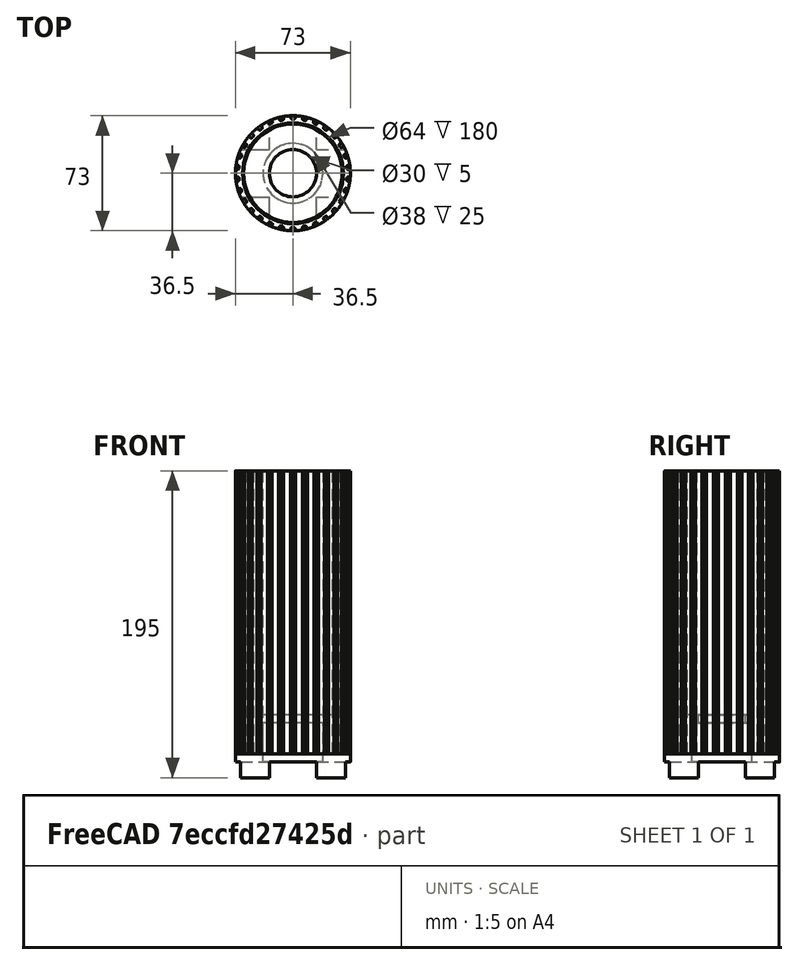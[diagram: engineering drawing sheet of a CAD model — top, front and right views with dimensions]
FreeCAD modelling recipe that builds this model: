
FCSTD DOCUMENT  (FreeCAD 0.15R4671 (Git))
Label: pica-small
License: All rights reserved
LicenseURL: http://en.wikipedia.org/wiki/All_rights_reserved
objects: Drawing::FeatureView×13, Part::Cylinder×7, Part::Cut×5, Drawing::FeatureViewPart×4, Part::MultiFuse×3, Part::Box×2, Part::Part2DObjectPython×1, PartDesign::Pad×1, Drawing::FeaturePage×1
note: 20 computed .brp shape members not serialized (recipe doc carries the construction recipe); baked Part::Feature solids carry a one-line shape summary decoded from their .brp

FEATURE [Part::Part2DObjectPython] InvoluteGear  # Draft 2D object (typed FeaturePython)
  ExternalGear = true
  HighPrecision = true
  Modules = 2.5
  NumberOfTeeth = 30
  PressureAngle = 20
FEATURE [PartDesign::Pad] Pad
  Length = 180
  Length2 = 100
  Sketch = -> InvoluteGear
  Type = 0
FEATURE [Part::Cylinder] Cylinder
  Angle = 360
  Height = 200
  Placement = pos=(0,0,-10) rot=(0,0,1;0rad)
  Radius = 32
FEATURE [Part::Cut] Cut  label="Final"
  Base = -> Pad
  Tool = -> Cylinder
FEATURE [Part::Cylinder] Cylinder001
  Angle = 360
  Height = 400
  Radius = 36.5
FEATURE [Part::Cylinder] Cylinder002
  Angle = 360
  Height = 400
  Radius = 100
FEATURE [Part::Cut] Cut001
  Base = -> Cylinder002
  Tool = -> Cylinder001
FEATURE [Part::Cut] Cut002  label="Shade"
  Base = -> Cut
  Placement = pos=(0,0,15) rot=(0,0,1;0rad)
  Tool = -> Cut001
FEATURE [Part::Cylinder] Cylinder003
  Angle = 360
  Height = 15
  Radius = 36.5
FEATURE [Part::Cylinder] Cylinder004
  Angle = 360
  Height = 40
  Radius = 31.3
FEATURE [Part::MultiFuse] Fusion  label="Base Fusion"
  Shapes = -> [Cylinder004,Cylinder003]
FEATURE [Part::Box] Box  label="Cube"
  Height = 10
  Length = 100
  Placement = pos=(-50,-15,0) rot=(0,0,1;0rad)
  Width = 30
FEATURE [Part::Box] Box001  label="Cube001"
  Height = 10
  Length = 100
  Placement = pos=(15,-50,0) rot=(0,0,1;1.5708rad)
  Width = 30
FEATURE [Part::MultiFuse] Fusion001  label="Feet Cutout Fusion"
  Shapes = -> [Box001,Box]
FEATURE [Part::Cut] Cut003  label="Plain Base"
  Base = -> Fusion
  Tool = -> Fusion001
FEATURE [Drawing::FeatureViewPart] FrontView  label="Shade Side"
  Direction = (0,-1,0)
  HiddenWidth = 0.15
  LineWidth = 0.35
  Rotation = 90
  ShowHiddenLines = true
  ShowSmoothLines = false
  Source = -> Cut002
  Tolerance = 0.05
  ViewResult = <blob: 110162 chars omitted>
  Visible = true
  X = 120
  Y = 230
FEATURE [Drawing::FeatureViewPart] View  label="Base Side"
  Direction = (0,-1,0)
  HiddenWidth = 0.15
  LineWidth = 0.35
  Rotation = 90
  ShowHiddenLines = false
  ShowSmoothLines = false
  Source = -> Cut003
  Tolerance = 0.05
  ViewResult = <blob: 2280 chars omitted>
  Visible = true
  X = 120
  Y = 260
FEATURE [Drawing::FeatureView] dim
  Rotation = 0
  ViewResult = <g   >\n<line x1="158.457700" y1="35.000000" x2="177.436492" y2="35.000000" style="stroke:rgb(0,0,0);stroke-width:0.30" />\n<line x1="158.432100" y1="215.000000" x2="177.436492" y2="215.000000" style="stroke:rgb(0,0,0);stroke-width:0.30" />\n<line x1="176.436492" y1="35.000000" x2="176.436492" y2="215.000000" style="stroke:rgb(0,0,0);stroke-width:0.30" />\n<polygon points="176.436492,35.000000 175.436492,38.000000 176.436492,39.000000 177.436492,38.000000" style="fill:rgb(0,0,0);stroke:rgb(0,0,0);stroke-width:0" /><polygon points="176.436492,215.000000 177.436492,212.000000 176.436492,211.000000 175.436492,212.000000" style="fill:rgb(0,0,0);stroke:rgb(0,0,0);stroke-width:0" />\n<text x="183.605138" y="123.622583" font-family="Arial" font-size="3.6" fill="rgb(0,0,0)" text-anchor="inherit" transform="rotate(-90.000000 183.605138,123.622583)" >180</text>\n</g> 
  Visible = true
  X = 0
  Y = 0
FEATURE [Drawing::FeatureView] dim001
  Rotation = 0
  ViewResult = <g   >\n<line x1="153.300000" y1="230.000000" x2="177.586905" y2="230.000000" style="stroke:rgb(0,0,0);stroke-width:0.30" />\n<line x1="158.500000" y1="245.000000" x2="177.586905" y2="245.000000" style="stroke:rgb(0,0,0);stroke-width:0.30" />\n<line x1="176.586905" y1="230.000000" x2="176.586905" y2="245.000000" style="stroke:rgb(0,0,0);stroke-width:0.30" />\n<polygon points="176.586905,230.000000 175.586905,233.000000 176.586905,234.000000 177.586905,233.000000" style="fill:rgb(0,0,0);stroke:rgb(0,0,0);stroke-width:0" /><polygon points="176.586905,245.000000 177.586905,242.000000 176.586905,241.000000 175.586905,242.000000" style="fill:rgb(0,0,0);stroke:rgb(0,0,0);stroke-width:0" />\n<text x="183.605138" y="239.198726" font-family="Arial" font-size="3.6" fill="rgb(0,0,0)" text-anchor="inherit" transform="rotate(-90.000000 183.605138,239.198726)" >15</text>\n</g> 
  Visible = false
  X = 0
  Y = 0
FEATURE [Drawing::FeatureView] dim002
  Rotation = 0
  ViewResult = <g   >\n<line x1="88.700000" y1="228.000000" x2="88.700000" y2="223.306199" style="stroke:rgb(0,0,0);stroke-width:0.30" />\n<line x1="151.300000" y1="228.000000" x2="151.300000" y2="223.306199" style="stroke:rgb(0,0,0);stroke-width:0.30" />\n<line x1="88.700000" y1="224.306199" x2="151.300000" y2="224.306199" style="stroke:rgb(0,0,0);stroke-width:0.30" />\n<polygon points="88.700000,224.306199 91.700000,225.306199 92.700000,224.306199 91.700000,223.306199" style="fill:rgb(0,0,0);stroke:rgb(0,0,0);stroke-width:0" /><polygon points="151.300000,224.306199 148.300000,223.306199 147.300000,224.306199 148.300000,225.306199" style="fill:rgb(0,0,0);stroke:rgb(0,0,0);stroke-width:0" />\n<text x="115.853258" y="222.009548" font-family="Arial" font-size="3.6" fill="rgb(0,0,0)" text-anchor="inherit" transform="rotate(0.000000 115.853258,222.009548)" >62.6</text>\n</g> 
  Visible = false
  X = 0
  Y = 0
FEATURE [Drawing::FeatureView] dim003
  Rotation = 0
  ViewResult = <g   >\n<line x1="81.500000" y1="245.000000" x2="71.574156" y2="245.000000" style="stroke:rgb(0,0,0);stroke-width:0.30" />\n<line x1="81.500000" y1="250.000000" x2="71.574156" y2="250.000000" style="stroke:rgb(0,0,0);stroke-width:0.30" />\n<line x1="72.574156" y1="245.000000" x2="72.574156" y2="250.000000" style="stroke:rgb(0,0,0);stroke-width:0.30" />\n<polygon points="72.574156,245.000000 73.574156,242.000000 72.574156,241.000000 71.574156,242.000000" style="fill:rgb(0,0,0);stroke:rgb(0,0,0);stroke-width:0" /><polygon points="72.574156,250.000000 71.574156,253.000000 72.574156,254.000000 73.574156,253.000000" style="fill:rgb(0,0,0);stroke:rgb(0,0,0);stroke-width:0" />\n<text x="69.103662" y="248.446547" font-family="Arial" font-size="3.6" fill="rgb(0,0,0)" text-anchor="inherit" transform="rotate(-90.000000 69.103662,248.446547)" >5</text>\n</g> 
  Visible = true
  X = 0
  Y = 0
FEATURE [Drawing::FeatureView] dim004
  Rotation = 0
  ViewResult = <g   >\n<line x1="86.700000" y1="230.000000" x2="58.179943" y2="230.000000" style="stroke:rgb(0,0,0);stroke-width:0.30" />\n<line x1="84.724600" y1="260.000000" x2="58.179943" y2="260.000000" style="stroke:rgb(0,0,0);stroke-width:0.30" />\n<line x1="59.179943" y1="230.000000" x2="59.179943" y2="260.000000" style="stroke:rgb(0,0,0);stroke-width:0.30" />\n<polygon points="59.179943,230.000000 58.179943,233.000000 59.179943,234.000000 60.179943,233.000000" style="fill:rgb(0,0,0);stroke:rgb(0,0,0);stroke-width:0" /><polygon points="59.179943,260.000000 60.179943,257.000000 59.179943,256.000000 58.179943,257.000000" style="fill:rgb(0,0,0);stroke:rgb(0,0,0);stroke-width:0" />\n<text x="55.878058" y="247.133410" font-family="Arial" font-size="3.6" fill="rgb(0,0,0)" text-anchor="inherit" transform="rotate(-90.000000 55.878058,247.133410)" >30</text>\n</g> 
  Visible = false
  X = 0
  Y = 0
FEATURE [Drawing::FeatureView] dim005
  Rotation = 0
  ViewResult = <g   >\n<line x1="86.724600" y1="262.000000" x2="86.724600" y2="275.781473" style="stroke:rgb(0,0,0);stroke-width:0.30" />\n<line x1="105.000000" y1="262.000000" x2="105.000000" y2="275.781473" style="stroke:rgb(0,0,0);stroke-width:0.30" />\n<line x1="86.724600" y1="274.781473" x2="105.000000" y2="274.781473" style="stroke:rgb(0,0,0);stroke-width:0.30" />\n<polygon points="86.724600,274.781473 89.724600,275.781473 90.724600,274.781473 89.724600,273.781473" style="fill:rgb(0,0,0);stroke:rgb(0,0,0);stroke-width:0" /><polygon points="105.000000,274.781473 102.000000,273.781473 101.000000,274.781473 102.000000,275.781473" style="fill:rgb(0,0,0);stroke:rgb(0,0,0);stroke-width:0" />\n<text x="90.028700" y="281.314168" font-family="Arial" font-size="3.6" fill="rgb(0,0,0)" text-anchor="inherit" transform="rotate(0.000000 90.028700,281.314168)" >18.275</text>\n</g> 
  Visible = true
  X = 0
  Y = 0
FEATURE [Drawing::FeatureViewPart] View001
  Direction = (0,0,1)
  HiddenWidth = 0.15
  LineWidth = 0.35
  Rotation = 0
  ShowHiddenLines = false
  ShowSmoothLines = false
  Source = -> Cut002
  Tolerance = 0.05
  ViewResult = <blob: 17329 chars omitted>
  Visible = true
  X = 300
  Y = 80
FEATURE [Drawing::FeatureView] dim006
  Rotation = 0
  ViewResult = <g   >\n <circle cx ="300.000000" cy ="170.000000" r="0.500000" stroke="none" fill="rgb(0,0,0)" /> \n<line x1="255.718312" y1="135.631286" x2="300.000000" y2="170.000000" style="stroke:rgb(0,0,0);stroke-width:0.30" />\n<polygon points="275.273643,150.808927 277.030448,153.438307 278.433561,153.261461 278.256715,151.858348" style="fill:rgb(0,0,0);stroke:rgb(0,0,0);stroke-width:0" />\n<line x1="255.718312" y1="135.631286" x2="231.639949" y2="135.631286" style="stroke:rgb(0,0,0);stroke-width:0.30" />\n<text x="219.448373" y="136.850443" font-family="Arial" font-size="3.6" fill="rgb(0,0,0)" text-anchor="inherit"  >R31.3</text>\n<!--31.3-->\n<!--R%3.3f-->\n</g> 
  Visible = true
  X = 0
  Y = 0
FEATURE [Drawing::FeatureView] centerLines
  Rotation = 0
  ViewResult = <g  transform="scale(1.000000,1.000000)" stroke="rgb(0,0,0)"  stroke-width="0.300000" >\n<path d="M 300.000000,170.000000 L 300.000000,168.000000 M 300.000000,166.000000 L 300.000000,160.000000 M 300.000000,158.000000 L 300.000000,156.000000 "/>\n<path d="M 300.000000,170.000000 L 302.000000,170.000000 M 304.000000,170.000000 L 310.000000,170.000000 M 312.000000,170.000000 L 314.000000,170.000000 "/>\n<path d="M 300.000000,170.000000 L 300.000000,172.000000 M 300.000000,174.000000 L 300.000000,180.000000 M 300.000000,182.000000 L 300.000000,184.000000 "/>\n<path d="M 300.000000,170.000000 L 298.000000,170.000000 M 296.000000,170.000000 L 290.000000,170.000000 M 288.000000,170.000000 L 286.000000,170.000000 "/>\n</g> 
  Visible = true
  X = 0
  Y = 0
FEATURE [Drawing::FeatureView] centerLines001
  Rotation = 0
  ViewResult = <g  transform="scale(1.000000,1.000000)" stroke="rgb(0,0,0)"  stroke-width="0.300000" >\n<path d="M 300.000000,80.000000 L 300.000000,82.000000 M 300.000000,84.000000 L 300.000000,90.000000 M 300.000000,92.000000 L 300.000000,94.000000 "/>\n<path d="M 300.000000,80.000000 L 302.000000,80.000000 M 304.000000,80.000000 L 310.000000,80.000000 M 312.000000,80.000000 L 314.000000,80.000000 "/>\n<path d="M 300.000000,80.000000 L 300.000000,78.000000 M 300.000000,76.000000 L 300.000000,70.000000 M 300.000000,68.000000 L 300.000000,66.000000 "/>\n<path d="M 300.000000,80.000000 L 298.000000,80.000000 M 296.000000,80.000000 L 290.000000,80.000000 M 288.000000,80.000000 L 286.000000,80.000000 "/>\n</g> 
  Visible = true
  X = 0
  Y = 0
FEATURE [Drawing::FeatureView] dim007
  Rotation = 0
  ViewResult = <g   >\n <circle cx ="300.000000" cy ="80.000000" r="0.500000" stroke="none" fill="rgb(0,0,0)" /> \n<line x1="340.917441" y1="111.884102" x2="300.000000" y2="80.000000" style="stroke:rgb(0,0,0);stroke-width:0.30" />\n<polygon points="325.241495,99.668933 323.489759,97.036174 322.086308,97.210316 322.260451,98.613767" style="fill:rgb(0,0,0);stroke:rgb(0,0,0);stroke-width:0" />\n<line x1="340.917441" y1="111.884102" x2="365.557939" y2="111.884102" style="stroke:rgb(0,0,0);stroke-width:0.30" />\n<text x="369.473360" y="112.835313" font-family="Arial" font-size="3.6" fill="rgb(0,0,0)" text-anchor="inherit"  >R32</text>\n<!--32.0-->\n<!--R%3.3f-->\n</g> 
  Visible = true
  X = 0
  Y = 0
FEATURE [Drawing::FeatureView] centerLines002
  Rotation = 0
  ViewResult = <blob: 2108 chars omitted>
  Visible = true
  X = 0
  Y = 0
FEATURE [Part::Cylinder] Cylinder005
  Angle = 360
  Height = 50
  Radius = 15
FEATURE [Part::Cylinder] Cylinder006
  Angle = 360
  Height = 35
  Radius = 19
FEATURE [Part::MultiFuse] Fusion002  label="Fixture Mount"
  Shapes = -> [Cylinder005,Cylinder006]
FEATURE [Part::Cut] Cut004  label="Base w/ Mount"
  Base = -> Cut003
  Tool = -> Fusion002
FEATURE [Drawing::FeatureViewPart] View003
  Direction = (0,0,1)
  HiddenWidth = 0.15
  LineWidth = 0.35
  Rotation = 0
  ShowHiddenLines = false
  ShowSmoothLines = false
  Source = -> Cut004
  Tolerance = 0.05
  ViewResult = <g id="View003"\n   transform="rotate(0,300,170) translate(300,170) scale(1,1)"\n  >\n<g   stroke="rgb(0, 0, 0)"\n   stroke-width="0.35"\n   stroke-linecap="butt"\n   stroke-linejoin="miter"\n   fill="none"\n   transform="scale(1,-1)"\n  >\n<circle cx ="0" cy ="0" r ="31.3" /><circle cx ="0" cy ="0" r ="15" /><circle cx ="0" cy ="0" r ="36.5" /></g>\n</g>
  Visible = true
  X = 300
  Y = 170
FEATURE [Drawing::FeatureView] dim008
  Rotation = 0
  ViewResult = <g   >\n<line x1="153.300000" y1="220.000000" x2="177.482857" y2="220.000000" style="stroke:rgb(0,0,0);stroke-width:0.30" />\n<line x1="158.500000" y1="245.000000" x2="177.482857" y2="245.000000" style="stroke:rgb(0,0,0);stroke-width:0.30" />\n<line x1="176.482857" y1="220.000000" x2="176.482857" y2="245.000000" style="stroke:rgb(0,0,0);stroke-width:0.30" />\n<polygon points="176.482857,220.000000 175.482857,223.000000 176.482857,224.000000 177.482857,223.000000" style="fill:rgb(0,0,0);stroke:rgb(0,0,0);stroke-width:0" /><polygon points="176.482857,245.000000 177.482857,242.000000 176.482857,241.000000 175.482857,242.000000" style="fill:rgb(0,0,0);stroke:rgb(0,0,0);stroke-width:0" />\n<text x="183.012587" y="234.189358" font-family="Arial" font-size="3.6" fill="rgb(0,0,0)" text-anchor="inherit" transform="rotate(-90.000000 183.012587,234.189358)" >25</text>\n</g> 
  Visible = true
  X = 0
  Y = 0
FEATURE [Drawing::FeatureView] dim009
  Rotation = 0
  ViewResult = <g   >\n<line x1="86.700000" y1="220.000000" x2="55.916145" y2="220.000000" style="stroke:rgb(0,0,0);stroke-width:0.30" />\n<line x1="84.724600" y1="260.000000" x2="55.916145" y2="260.000000" style="stroke:rgb(0,0,0);stroke-width:0.30" />\n<line x1="56.916145" y1="220.000000" x2="56.916145" y2="260.000000" style="stroke:rgb(0,0,0);stroke-width:0.30" />\n<polygon points="56.916145,220.000000 55.916145,223.000000 56.916145,224.000000 57.916145,223.000000" style="fill:rgb(0,0,0);stroke:rgb(0,0,0);stroke-width:0" /><polygon points="56.916145,260.000000 57.916145,257.000000 56.916145,256.000000 55.916145,257.000000" style="fill:rgb(0,0,0);stroke:rgb(0,0,0);stroke-width:0" />\n<text x="53.319214" y="242.898641" font-family="Arial" font-size="3.6" fill="rgb(0,0,0)" text-anchor="inherit" transform="rotate(-90.000000 53.319214,242.898641)" >40</text>\n</g> 
  Visible = true
  X = 0
  Y = 0
FEATURE [Drawing::FeaturePage] AutoDrawing  label="Initial Sketch"
  EditableTexts = FLOYD DIEBEL | 7/25/2015 | 1:1 | 1 | 1 | PICA (SMALL) | LAMP WITH SHADE
  Group = -> [FrontView,View,dim,dim001,dim002,dim003,dim004,dim005,View001,dim006,centerLines,centerLines001,dim007,centerLines002,View003,dim008,dim009]
  Template = C:/Program Files/FreeCAD 0.15/data/Mod/Drawing/Templates/A3_Landscape.svg
